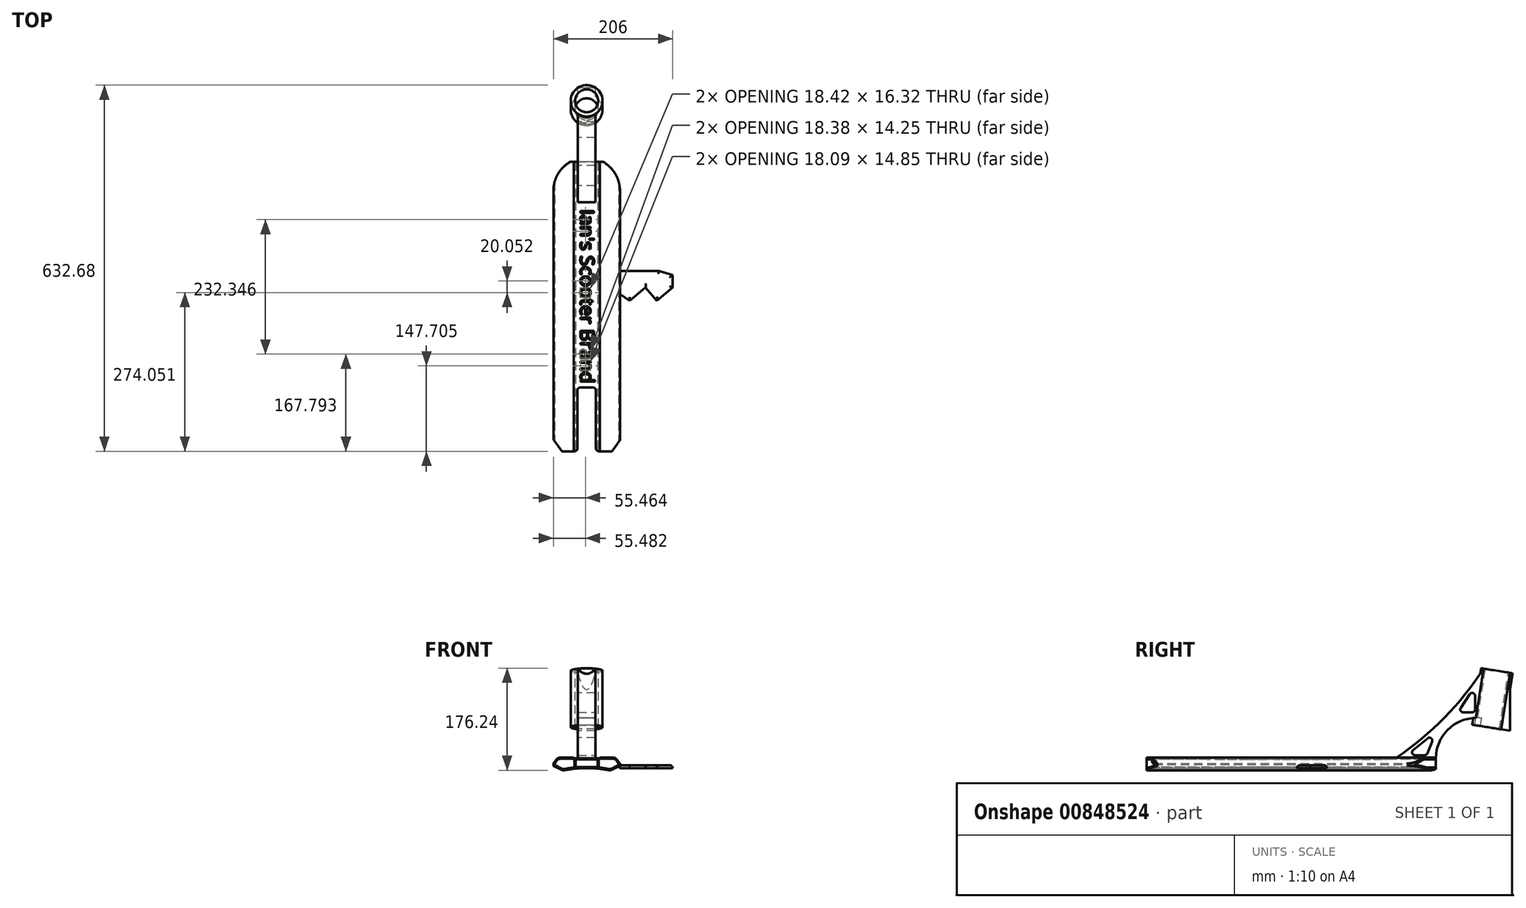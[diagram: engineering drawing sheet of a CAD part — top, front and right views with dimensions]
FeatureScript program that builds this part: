
annotation { "Feature Type Name" : "Feature", "Feature Type Description" : "" }
export const myFeature = defineFeature(function(context is Context, id is Id, definition is map)
    precondition{}
    {
        {
            var Q0;
            Q0=qCreatedBy(makeId("Front.planeOp"),FACE);
            var sketch = newSketch(context, id + "F0", { "sketchPlane" : qUnion([Q0])});
            skLineSegment(sketch, "E0", {"start": v(0, 52.1) * mm, "end": v(0, -52.5) * mm, "construction": true});
            skLineSegment(sketch, "E1", {"start": v(0, 16.68) * mm, "end": v(22.5, 16.68) * mm});
            skLineSegment(sketch, "E2", {"start": v(22.5, 16.68) * mm, "end": v(22.5, 17.98) * mm});
            skLineSegment(sketch, "E3", {"start": v(22.5, 17.98) * mm, "end": v(50.12, 17.98) * mm});
            skLineSegment(sketch, "E4", {"start": v(50.12, 17.98) * mm, "end": v(57.5, 7.98) * mm});
            skLineSegment(sketch, "E5", {"start": v(57.5, 7.98) * mm, "end": v(57.5, 3.98) * mm});
            skLineSegment(sketch, "E6", {"start": v(57.5, 3.98) * mm, "end": v(41.14, -4.28) * mm});
            skLineSegment(sketch, "E7.MirrorCS", {"start": v(0, 16.68) * mm, "end": v(-22.5, 16.68) * mm});
            skLineSegment(sketch, "E8.MirrorCS", {"start": v(-22.5, 17.98) * mm, "end": v(-50.12, 17.98) * mm});
            skLineSegment(sketch, "E9.MirrorCS", {"start": v(-22.5, 16.68) * mm, "end": v(-22.5, 17.98) * mm});
            skLineSegment(sketch, "E10.MirrorCS", {"start": v(-50.12, 17.98) * mm, "end": v(-57.5, 7.98) * mm});
            skLineSegment(sketch, "E11.MirrorCS", {"start": v(-57.5, 7.98) * mm, "end": v(-57.5, 3.98) * mm});
            skLineSegment(sketch, "E12.MirrorCS", {"start": v(-57.5, 3.98) * mm, "end": v(-41.14, -4.28) * mm});
            skArc(sketch, "E13", {"start": v(41.14, -4.28) * mm, "mid": v(0, 0) * mm, "end": v(-41.14, -4.28) * mm});
            skSolve(sketch);
        }
        {
            var Q0;
            Q0 = qSketchRegion(id + "F0", true);
            extrude(context, id + "F1", {"entities" : qUnion([Q0]), "endBound" : BoundingType.SYMMETRIC, "depth" : 500 * mm, "offsetDistance" : 25 * mm});
        }
        {
            var Q0;
            Q0=makeQuery(id+"F1.opExtrude","CAP_FACE",FACE,{"disambiguationData":[OSD([sQuery(id+"F0.wireOp",EDGE,"E1"),sQuery(id+"F0.wireOp",EDGE,"E2"),sQuery(id+"F0.wireOp",EDGE,"E3"),sQuery(id+"F0.wireOp",EDGE,"E4"),sQuery(id+"F0.wireOp",EDGE,"E5"),sQuery(id+"F0.wireOp",EDGE,"E6"),sQuery(id+"F0.wireOp",EDGE,"E7.MirrorCS"),sQuery(id+"F0.wireOp",EDGE,"E8.MirrorCS"),sQuery(id+"F0.wireOp",EDGE,"E9.MirrorCS"),sQuery(id+"F0.wireOp",EDGE,"E10.MirrorCS"),sQuery(id+"F0.wireOp",EDGE,"E11.MirrorCS"),sQuery(id+"F0.wireOp",EDGE,"E12.MirrorCS"),sQuery(id+"F0.wireOp",EDGE,"E13")])],"isStart":false});
            var sketch = newSketch(context, id + "F2", { "sketchPlane" : qUnion([Q0])});
            skLineSegment(sketch, "E14.bottom", {"start": v(19, 14.68) * mm, "end": v(-19, 14.68) * mm});
            skLineSegment(sketch, "E14.top", {"start": v(19, 1.68) * mm, "end": v(-19, 1.68) * mm});
            skLineSegment(sketch, "E14.left", {"start": v(19, 14.68) * mm, "end": v(19, 1.68) * mm});
            skLineSegment(sketch, "E14.right", {"start": v(-19, 14.68) * mm, "end": v(-19, 1.68) * mm});
            skPoint(sketch, "E14.middle", {"position": v(0, 8.18) * mm});
            skSolve(sketch);
        }
        {
            var Q0;
            Q0=makeQuery(id+"F2.imprint","IMPRINT",FACE,{"disambiguationData":[TD([[makeQuery(id+"F2.imprint","IMPRINT",EDGE,{"derivedFrom":sQuery(id+"F2.wireOp",EDGE,"E14.bottom")}),1.0]])]});
            extrude(context, id + "F3", {"entities" : qUnion([Q0]), "operationType" : NewBodyOperationType.REMOVE, "oppositeDirection" : true, "depth" : 1000 * mm, "offsetDistance" : 25 * mm});
        }
        {
            var Q0;
            Q0=makeQuery(id+"F1.opExtrude","SWEPT_EDGE",EDGE,{"disambiguationData":[OSD([sQuery(id+"F0.wireOp",EDGE,"E8.MirrorCS"),sQuery(id+"F0.wireOp",EDGE,"E9.MirrorCS")])]});
            var Q1;
            Q1=makeQuery(id+"F1.opExtrude","SWEPT_EDGE",EDGE,{"disambiguationData":[OSD([sQuery(id+"F0.wireOp",EDGE,"E2"),sQuery(id+"F0.wireOp",EDGE,"E3")])]});
            fillet(context, id + "F4", {"entities" : qUnion([Q0, Q1]), "radius" : 1 * mm, "tangentPropagation" : true, "allowEdgeOverflow" : false});
        }
        {
            var Q0;
            Q0=makeQuery(id+"F1.opExtrude","SWEPT_EDGE",EDGE,{"disambiguationData":[OSD([sQuery(id+"F0.wireOp",EDGE,"E8.MirrorCS"),sQuery(id+"F0.wireOp",EDGE,"E10.MirrorCS")])]});
            var Q1;
            Q1=makeQuery(id+"F1.opExtrude","SWEPT_EDGE",EDGE,{"disambiguationData":[OSD([sQuery(id+"F0.wireOp",EDGE,"E3"),sQuery(id+"F0.wireOp",EDGE,"E4")])]});
            var Q2;
            Q2=makeQuery(id+"F1.opExtrude","SWEPT_EDGE",EDGE,{"disambiguationData":[OSD([sQuery(id+"F0.wireOp",EDGE,"E6"),sQuery(id+"F0.wireOp",EDGE,"E13")])]});
            var Q3;
            Q3=makeQuery(id+"F1.opExtrude","SWEPT_EDGE",EDGE,{"disambiguationData":[OSD([sQuery(id+"F0.wireOp",EDGE,"E12.MirrorCS"),sQuery(id+"F0.wireOp",EDGE,"E13")])]});
            fillet(context, id + "F5", {"entities" : qUnion([Q0, Q1, Q2, Q3]), "radius" : 9 * mm, "tangentPropagation" : true, "allowEdgeOverflow" : false});
        }
        {
            var Q0;
            Q0=makeQuery(id+"F1.opExtrude","SWEPT_EDGE",EDGE,{"disambiguationData":[OSD([sQuery(id+"F0.wireOp",EDGE,"E10.MirrorCS"),sQuery(id+"F0.wireOp",EDGE,"E11.MirrorCS")])]});
            var Q1;
            Q1=makeQuery(id+"F1.opExtrude","SWEPT_EDGE",EDGE,{"disambiguationData":[OSD([sQuery(id+"F0.wireOp",EDGE,"E11.MirrorCS"),sQuery(id+"F0.wireOp",EDGE,"E12.MirrorCS")])]});
            var Q2;
            Q2=makeQuery(id+"F1.opExtrude","SWEPT_EDGE",EDGE,{"disambiguationData":[OSD([sQuery(id+"F0.wireOp",EDGE,"E4"),sQuery(id+"F0.wireOp",EDGE,"E5")])]});
            var Q3;
            Q3=makeQuery(id+"F1.opExtrude","SWEPT_EDGE",EDGE,{"disambiguationData":[OSD([sQuery(id+"F0.wireOp",EDGE,"E5"),sQuery(id+"F0.wireOp",EDGE,"E6")])]});
            fillet(context, id + "F6", {"entities" : qUnion([Q0, Q1, Q2, Q3]), "radius" : 1 * mm, "tangentPropagation" : true, "allowEdgeOverflow" : false});
        }
        {
            var Q0;
            Q0=makeQuery(id+"F1.opExtrude","CAP_FACE",FACE,{"disambiguationData":[OSD([sQuery(id+"F0.wireOp",EDGE,"E1"),sQuery(id+"F0.wireOp",EDGE,"E2"),sQuery(id+"F0.wireOp",EDGE,"E3"),sQuery(id+"F0.wireOp",EDGE,"E4"),sQuery(id+"F0.wireOp",EDGE,"E5"),sQuery(id+"F0.wireOp",EDGE,"E6"),sQuery(id+"F0.wireOp",EDGE,"E7.MirrorCS"),sQuery(id+"F0.wireOp",EDGE,"E8.MirrorCS"),sQuery(id+"F0.wireOp",EDGE,"E9.MirrorCS"),sQuery(id+"F0.wireOp",EDGE,"E10.MirrorCS"),sQuery(id+"F0.wireOp",EDGE,"E11.MirrorCS"),sQuery(id+"F0.wireOp",EDGE,"E12.MirrorCS"),sQuery(id+"F0.wireOp",EDGE,"E13")])],"isStart":false});
            var sketch = newSketch(context, id + "F7", { "sketchPlane" : qUnion([Q0])});
            skArc(sketch, "E15.0", {"start": v(-21, 0.9) * mm, "mid": v(-29.8, -0.2) * mm, "end": v(-38.53, -1.7) * mm});
            skArc(sketch, "E15.1", {"start": v(-43.02, -1.09) * mm, "mid": v(-40.83, -1.77) * mm, "end": v(-38.53, -1.7) * mm});
            skLineSegment(sketch, "E15.2", {"start": v(-55.5, 5.21) * mm, "end": v(-43.02, -1.09) * mm});
            skLineSegment(sketch, "E15.3", {"start": v(-23.5, 15.98) * mm, "end": v(-45.57, 15.98) * mm});
            skArc(sketch, "E15.4", {"start": v(-45.57, 15.98) * mm, "mid": v(-48.73, 15.23) * mm, "end": v(-51.2, 13.14) * mm});
            skLineSegment(sketch, "E15.5", {"start": v(-51.2, 13.14) * mm, "end": v(-55.5, 7.32) * mm});
            skLineSegment(sketch, "E15.6", {"start": v(-55.5, 7.32) * mm, "end": v(-55.5, 5.21) * mm});
            skLineSegment(sketch, "E16.0", {"start": v(-21, 14.68) * mm, "end": v(-21, 0.54) * mm});
            skLineSegment(sketch, "E17.0", {"start": v(-22.5, 14.68) * mm, "end": v(-21, 14.68) * mm});
            skLineSegment(sketch, "E18", {"start": v(-23.5, 15.98) * mm, "end": v(-22.5, 14.68) * mm});
            skLineSegment(sketch, "E19.MirrorCS", {"start": v(21, 14.68) * mm, "end": v(21, 0.54) * mm});
            skLineSegment(sketch, "E20.MirrorCS", {"start": v(22.5, 14.68) * mm, "end": v(21, 14.68) * mm});
            skLineSegment(sketch, "E21.MirrorCS", {"start": v(23.5, 15.98) * mm, "end": v(45.57, 15.98) * mm});
            skArc(sketch, "E22.MirrorCS", {"start": v(45.57, 15.98) * mm, "mid": v(48.73, 15.23) * mm, "end": v(51.2, 13.14) * mm});
            skLineSegment(sketch, "E23.MirrorCS", {"start": v(51.2, 13.14) * mm, "end": v(55.5, 7.32) * mm});
            skLineSegment(sketch, "E24.MirrorCS", {"start": v(23.5, 15.98) * mm, "end": v(22.5, 14.68) * mm});
            skLineSegment(sketch, "E25.MirrorCS", {"start": v(55.5, 5.21) * mm, "end": v(43.02, -1.09) * mm});
            skArc(sketch, "E26.MirrorCS", {"start": v(21, 0.9) * mm, "mid": v(29.8, -0.2) * mm, "end": v(38.53, -1.7) * mm});
            skArc(sketch, "E27.MirrorCS", {"start": v(43.02, -1.09) * mm, "mid": v(40.83, -1.77) * mm, "end": v(38.53, -1.7) * mm});
            skLineSegment(sketch, "E28.MirrorCS", {"start": v(55.5, 7.32) * mm, "end": v(55.5, 5.21) * mm});
            skSolve(sketch);
        }
        {
            var Q0;
            {var subQ0=sQuery(id+"F7.wireOp",EDGE,"E15.0");Q0=makeQuery(id+"F7.imprint","IMPRINT",FACE,{"disambiguationData":[TD([[makeQuery(id+"F7.imprint","IMPRINT",EDGE,{"derivedFrom":subQ0}),-1.0]])]});}
            var Q1;
            {var subQ0=sQuery(id+"F7.wireOp",EDGE,"E20.MirrorCS");Q1=makeQuery(id+"F7.imprint","IMPRINT",FACE,{"disambiguationData":[TD([[makeQuery(id+"F7.imprint","IMPRINT",EDGE,{"derivedFrom":subQ0}),1.0]])]});}
            extrude(context, id + "F8", {"entities" : qUnion([Q0, Q1]), "operationType" : NewBodyOperationType.REMOVE, "oppositeDirection" : true, "depth" : 1000 * mm, "offsetDistance" : 25 * mm});
        }
        {
            var Q0;
            Q0=makeQuery(id+"F1.opExtrude","SWEPT_FACE",FACE,{"disambiguationData":[OSD([sQuery(id+"F0.wireOp",EDGE,"E8.MirrorCS")])]});
            var sketch = newSketch(context, id + "F9", { "sketchPlane" : qUnion([Q0])});
            skCircle(sketch, "E29", {"center": v(0, 200) * mm, "radius": 57.5 * mm});
            skLineSegment(sketch, "E30", {"start": v(-57.5, 200) * mm, "end": v(-57.5, 280) * mm});
            skLineSegment(sketch, "E31", {"start": v(-57.5, 280) * mm, "end": v(57.5, 280) * mm});
            skLineSegment(sketch, "E32", {"start": v(57.5, 280) * mm, "end": v(57.5, 200) * mm});
            skSolve(sketch);
        }
        {
            var Q0;
            {var subQ0=sQuery(id+"F9.wireOp",EDGE,"E30");Q0=makeQuery(id+"F9.imprint","IMPRINT",FACE,{"disambiguationData":[TD([[makeQuery(id+"F9.imprint","IMPRINT",EDGE,{"derivedFrom":subQ0}),-1.0]])]});}
            var Q1;
            {var subQ0=sQuery(id+"F9.wireOp",EDGE,"E29");var subQ1=sQuery(id+"F0.wireOp",EDGE,"E8.MirrorCS");var subQ2=makeQuery(id+"F1.opExtrude","CAP_EDGE",EDGE,{"disambiguationData":[OSD([subQ1])],"isStart":true});var subQ3=makeQuery(id+"F9.imprint","INTERSECT",VERTEX,{"derivedFrom":[subQ2,subQ0]});Q1=makeQuery(id+"F9.imprint","IMPRINT",FACE,{"disambiguationData":[TD([[makeQuery(id+"F9.imprint","IMPRINT",EDGE,{"disambiguationData":[TD([[subQ3,-1.0]])],"derivedFrom":subQ0}),-1.0]])]});}
            extrude(context, id + "F10", {"entities" : qUnion([Q0, Q1]), "operationType" : NewBodyOperationType.REMOVE, "endBound" : BoundingType.THROUGH_ALL, "depth" : 25 * mm, "offsetDistance" : 25 * mm, "hasSecondDirection" : true, "secondDirectionBound" : SecondDirectionBoundingType.THROUGH_ALL, "secondDirectionOppositeDirection" : true, "secondDirectionDepth" : 25 * mm});
        }
        {
            var Q0;
            Q0=makeQuery(id+"F1.opExtrude","SWEPT_FACE",FACE,{"disambiguationData":[OSD([sQuery(id+"F0.wireOp",EDGE,"E8.MirrorCS")])]});
            var sketch = newSketch(context, id + "F11", { "sketchPlane" : qUnion([Q0])});
            skLineSegment(sketch, "E33", {"start": v(-16, -250.16) * mm, "end": v(-16, -140) * mm});
            skLineSegment(sketch, "E34", {"start": v(-16, -140) * mm, "end": v(16, -140) * mm});
            skLineSegment(sketch, "E35", {"start": v(16, -140) * mm, "end": v(16, -250) * mm});
            skLineSegment(sketch, "E36", {"start": v(16, -250) * mm, "end": v(43.9, -250) * mm});
            skLineSegment(sketch, "E37", {"start": v(43.9, -250) * mm, "end": v(68.6, -216) * mm});
            skLineSegment(sketch, "E38", {"start": v(68.6, -216) * mm, "end": v(68.6, -346) * mm});
            skLineSegment(sketch, "E39", {"start": v(68.6, -346) * mm, "end": v(-67.4, -346) * mm});
            skLineSegment(sketch, "E40", {"start": v(-67.4, -346) * mm, "end": v(-67.4, -216) * mm});
            skLineSegment(sketch, "E41", {"start": v(-67.4, -216) * mm, "end": v(-42.7, -250) * mm});
            skLineSegment(sketch, "E42", {"start": v(-42.7, -250) * mm, "end": v(-16, -250.16) * mm});
            skSolve(sketch);
        }
        {
            var Q0;
            Q0=makeQuery(id+"F11.imprint","IMPRINT",FACE,{"disambiguationData":[TD([[makeQuery(id+"F11.imprint","IMPRINT",EDGE,{"derivedFrom":sQuery(id+"F11.wireOp",EDGE,"E33")}),-1.0]])]});
            var Q1;
            {var subQ0=sQuery(id+"F11.wireOp",EDGE,"E41");var subQ1=sQuery(id+"F0.wireOp",EDGE,"E8.MirrorCS");var subQ2=makeQuery(id+"F1.opExtrude","CAP_EDGE",EDGE,{"disambiguationData":[OSD([subQ1])],"isStart":false});var subQ3=makeQuery(id+"F11.imprint","INTERSECT",VERTEX,{"derivedFrom":[subQ2,subQ0,sQuery(id+"F11.wireOp",EDGE,"E42")]});Q1=makeQuery(id+"F11.imprint","IMPRINT",FACE,{"disambiguationData":[TD([[makeQuery(id+"F11.imprint","IMPRINT",EDGE,{"disambiguationData":[TD([[subQ3,1.0]])],"derivedFrom":subQ0}),-1.0]])]});}
            extrude(context, id + "F12", {"entities" : qUnion([Q0, Q1]), "operationType" : NewBodyOperationType.REMOVE, "endBound" : BoundingType.THROUGH_ALL, "oppositeDirection" : true, "depth" : 25 * mm, "offsetDistance" : 25 * mm, "hasSecondDirection" : true, "secondDirectionBound" : SecondDirectionBoundingType.THROUGH_ALL, "secondDirectionOppositeDirection" : false, "secondDirectionDepth" : 25 * mm});
        }
        {
            var Q0;
            {var subQ0=sQuery(id+"F11.wireOp",EDGE,"E34");var subQ1=sQuery(id+"F11.wireOp",EDGE,"E33");Q0=makeQuery(id+"F12.boolean.opBoolean","COPY",EDGE,{"disambiguationData":[TD([makeQuery(id+"F3.boolean.opBoolean","COPY",FACE,{"derivedFrom":makeQuery(id+"F3.opExtrude","SWEPT_FACE",FACE,{"disambiguationData":[OSD([sQuery(id+"F2.wireOp",EDGE,"E14.bottom")])]})})])],"derivedFrom":makeQuery(id+"F12.opExtrude","SWEPT_EDGE",EDGE,{"disambiguationData":[OSD([subQ1,subQ0])]})});}
            var Q1;
            {var subQ0=sQuery(id+"F11.wireOp",EDGE,"E33");var subQ1=sQuery(id+"F11.wireOp",EDGE,"E34");Q1=makeQuery(id+"F12.boolean.opBoolean","COPY",EDGE,{"disambiguationData":[TD([makeQuery(id+"F1.opExtrude","SWEPT_FACE",FACE,{"disambiguationData":[OSD([sQuery(id+"F0.wireOp",EDGE,"E13")])]})])],"derivedFrom":makeQuery(id+"F12.opExtrude","SWEPT_EDGE",EDGE,{"disambiguationData":[OSD([subQ0,subQ1])]})});}
            var Q2;
            {var subQ0=sQuery(id+"F11.wireOp",EDGE,"E34");var subQ1=sQuery(id+"F11.wireOp",EDGE,"E35");Q2=makeQuery(id+"F12.boolean.opBoolean","COPY",EDGE,{"disambiguationData":[TD([makeQuery(id+"F3.boolean.opBoolean","COPY",FACE,{"derivedFrom":makeQuery(id+"F3.opExtrude","SWEPT_FACE",FACE,{"disambiguationData":[OSD([sQuery(id+"F2.wireOp",EDGE,"E14.bottom")])]})})])],"derivedFrom":makeQuery(id+"F12.opExtrude","SWEPT_EDGE",EDGE,{"disambiguationData":[OSD([subQ0,subQ1])]})});}
            var Q3;
            {var subQ0=sQuery(id+"F11.wireOp",EDGE,"E35");var subQ1=sQuery(id+"F11.wireOp",EDGE,"E34");Q3=makeQuery(id+"F12.boolean.opBoolean","COPY",EDGE,{"disambiguationData":[TD([makeQuery(id+"F1.opExtrude","SWEPT_FACE",FACE,{"disambiguationData":[OSD([sQuery(id+"F0.wireOp",EDGE,"E13")])]})])],"derivedFrom":makeQuery(id+"F12.opExtrude","SWEPT_EDGE",EDGE,{"disambiguationData":[OSD([subQ1,subQ0])]})});}
            var Q4;
            {var subQ2=sQuery(id+"F11.wireOp",EDGE,"E35");Q4=makeQuery(id+"F12.boolean.opBoolean","COPY",EDGE,{"disambiguationData":[TD([makeQuery(id+"F3.boolean.opBoolean","COPY",FACE,{"derivedFrom":makeQuery(id+"F3.opExtrude","SWEPT_FACE",FACE,{"disambiguationData":[OSD([sQuery(id+"F2.wireOp",EDGE,"E14.bottom")])]})})])],"derivedFrom":makeQuery(id+"F12.opExtrude","SWEPT_EDGE",EDGE,{"disambiguationData":[OSD([subQ2,sQuery(id+"F11.wireOp",EDGE,"E36")])]})});}
            var Q5;
            Q5=makeQuery(id+"F12.boolean.opBoolean","INTERSECT",EDGE,{"disambiguationData":[OD(0.0)],"derivedFrom":[makeQuery(id+"F1.opExtrude","CAP_FACE",FACE,{"disambiguationData":[OSD([sQuery(id+"F0.wireOp",EDGE,"E1"),sQuery(id+"F0.wireOp",EDGE,"E2"),sQuery(id+"F0.wireOp",EDGE,"E3"),sQuery(id+"F0.wireOp",EDGE,"E4"),sQuery(id+"F0.wireOp",EDGE,"E5"),sQuery(id+"F0.wireOp",EDGE,"E6"),sQuery(id+"F0.wireOp",EDGE,"E7.MirrorCS"),sQuery(id+"F0.wireOp",EDGE,"E8.MirrorCS"),sQuery(id+"F0.wireOp",EDGE,"E9.MirrorCS"),sQuery(id+"F0.wireOp",EDGE,"E10.MirrorCS"),sQuery(id+"F0.wireOp",EDGE,"E11.MirrorCS"),sQuery(id+"F0.wireOp",EDGE,"E12.MirrorCS"),sQuery(id+"F0.wireOp",EDGE,"E13")])],"isStart":false}),makeQuery(id+"F12.opExtrude","SWEPT_FACE",FACE,{"disambiguationData":[OSD([sQuery(id+"F11.wireOp",EDGE,"E33")])]})]});
            fillet(context, id + "F13", {"entities" : qUnion([Q0, Q1, Q2, Q3, Q4, Q5]), "radius" : 5 * mm, "tangentPropagation" : true, "allowEdgeOverflow" : false});
        }
        {
            var Q0;
            Q0=qCreatedBy(makeId("Right.planeOp"),FACE);
            var sketch = newSketch(context, id + "F14", { "sketchPlane" : qUnion([Q0])});
            skLineSegment(sketch, "E43", {"start": v(250.22, 16.68) * mm, "end": v(180.22, 16.68) * mm});
            skLineSegment(sketch, "E44", {"start": v(332.8, 85.54) * mm, "end": v(332.8, 71.7) * mm});
            skLineSegment(sketch, "E45", {"start": v(332.8, 71.7) * mm, "end": v(378.23, 64.5) * mm});
            skLineSegment(sketch, "E46", {"start": v(378.23, 64.5) * mm, "end": v(378.23, 164.5) * mm});
            skLineSegment(sketch, "E47", {"start": v(378.23, 164.5) * mm, "end": v(332.8, 171.7) * mm});
            skArc(sketch, "E48", {"start": v(180.22, 16.68) * mm, "mid": v(264.25, 86.57) * mm, "end": v(332.8, 171.7) * mm});
            skArc(sketch, "E49", {"start": v(332.8, 85.54) * mm, "mid": v(275.4, 70.44) * mm, "end": v(250.22, 16.68) * mm});
            skSolve(sketch);
        }
        {
            var Q0;
            Q0=makeQuery(id+"F14.imprint","IMPRINT",FACE,{"disambiguationData":[TD([[makeQuery(id+"F14.imprint","IMPRINT",EDGE,{"derivedFrom":sQuery(id+"F14.wireOp",EDGE,"E43")}),-1.0]])]});
            extrude(context, id + "F15", {"entities" : qUnion([Q0]), "operationType" : NewBodyOperationType.ADD, "endBound" : BoundingType.SYMMETRIC, "depth" : 30 * mm, "offsetDistance" : 25 * mm});
        }
        {
            var Q0;
            Q0=makeQuery(id+"F15.opExtrude","SWEPT_FACE",FACE,{"disambiguationData":[OSD([sQuery(id+"F14.wireOp",EDGE,"E47")])]});
            var sketch = newSketch(context, id + "F16", { "sketchPlane" : qUnion([Q0])});
            skCircle(sketch, "E50", {"center": v(0, 324.85) * mm, "radius": 27.5 * mm});
            skPoint(sketch, "E50.centerSnap0", {"position": v(15, 324.85) * mm});
            skSolve(sketch);
        }
        {
            var Q0;
            Q0=makeQuery(id+"F16.imprint","IMPRINT",FACE,{"disambiguationData":[TD([[makeQuery(id+"F16.imprint","IMPRINT",EDGE,{"derivedFrom":sQuery(id+"F16.wireOp",EDGE,"E50")}),1.0]])]});
            var Q1;
            Q1=makeQuery(id+"F15.opExtrude","SWEPT_FACE",FACE,{"disambiguationData":[OSD([sQuery(id+"F14.wireOp",EDGE,"E45")])]});
            extrude(context, id + "F17", {"entities" : qUnion([Q0]), "operationType" : NewBodyOperationType.ADD, "endBound" : BoundingType.UP_TO_SURFACE, "oppositeDirection" : true, "depth" : 25 * mm, "endBoundEntityFace" : qUnion([Q1]), "offsetDistance" : 25 * mm});
        }
        {
            var Q0;
            {var subQ0=sQuery(id+"F14.wireOp",EDGE,"E47");Q0=makeQuery(id+"F17.boolean.opBoolean","MERGE",FACE,{"derivedFrom":[makeQuery(id+"F15.opExtrude","SWEPT_FACE",FACE,{"disambiguationData":[OSD([subQ0])]}),makeQuery(id+"F17.opExtrude","CAP_FACE",FACE,{"disambiguationData":[OSD([sQuery(id+"F14.wireOp",EDGE,"E46"),subQ0,sQuery(id+"F14.wireOp",EDGE,"E48"),sQuery(id+"F16.wireOp",EDGE,"E50")])],"isStart":true})]});}
            var sketch = newSketch(context, id + "F18", { "sketchPlane" : qUnion([Q0])});
            skPoint(sketch, "E51", {"position": v(0, 324.85) * mm});
            skSolve(sketch);
        }
        {
            var Q0;
            Q0=sQuery(id+"F18.wireOp",VERTEX,"E51");
            var Q1;
            Q1=makeQuery(id+"F1.opExtrude","SWEPT_BODY",BODY,{"disambiguationData":[OSD([sQuery(id+"F0.wireOp",EDGE,"E1"),sQuery(id+"F0.wireOp",EDGE,"E2"),sQuery(id+"F0.wireOp",EDGE,"E3"),sQuery(id+"F0.wireOp",EDGE,"E4"),sQuery(id+"F0.wireOp",EDGE,"E5"),sQuery(id+"F0.wireOp",EDGE,"E6"),sQuery(id+"F0.wireOp",EDGE,"E7.MirrorCS"),sQuery(id+"F0.wireOp",EDGE,"E8.MirrorCS"),sQuery(id+"F0.wireOp",EDGE,"E9.MirrorCS"),sQuery(id+"F0.wireOp",EDGE,"E10.MirrorCS"),sQuery(id+"F0.wireOp",EDGE,"E11.MirrorCS"),sQuery(id+"F0.wireOp",EDGE,"E12.MirrorCS"),sQuery(id+"F0.wireOp",EDGE,"E13")])]});
            hole(context, id + "F19", {"style" : HoleStyle.SIMPLE, "endStyle" : HoleEndStyle.THROUGH, "holeDiameter" : 40 * mm, "majorDiameter" : 5 * mm, "isTappedThrough" : true, "tappedDepth" : 12 * mm, "tapClearance" : 3, "locations" : qUnion([Q0]), "scope" : qUnion([Q1])});
        }
        {
            var Q0;
            Q0=makeQuery(id+"F8.boolean.opBoolean","COPY",FACE,{"derivedFrom":makeQuery(id+"F8.opExtrude","SWEPT_FACE",FACE,{"disambiguationData":[OSD([sQuery(id+"F7.wireOp",EDGE,"E19.MirrorCS")])]})});
            var sketch = newSketch(context, id + "F20", { "sketchPlane" : qUnion([Q0])});
            skPoint(sketch, "E52", {"position": v(-236, 10.9) * mm});
            skSolve(sketch);
        }
        {
            var Q0;
            Q0=sQuery(id+"F20.wireOp",VERTEX,"E52");
            var Q1;
            Q1=makeQuery(id+"F1.opExtrude","SWEPT_BODY",BODY,{"disambiguationData":[OSD([sQuery(id+"F0.wireOp",EDGE,"E1"),sQuery(id+"F0.wireOp",EDGE,"E2"),sQuery(id+"F0.wireOp",EDGE,"E3"),sQuery(id+"F0.wireOp",EDGE,"E4"),sQuery(id+"F0.wireOp",EDGE,"E5"),sQuery(id+"F0.wireOp",EDGE,"E6"),sQuery(id+"F0.wireOp",EDGE,"E7.MirrorCS"),sQuery(id+"F0.wireOp",EDGE,"E8.MirrorCS"),sQuery(id+"F0.wireOp",EDGE,"E9.MirrorCS"),sQuery(id+"F0.wireOp",EDGE,"E10.MirrorCS"),sQuery(id+"F0.wireOp",EDGE,"E11.MirrorCS"),sQuery(id+"F0.wireOp",EDGE,"E12.MirrorCS"),sQuery(id+"F0.wireOp",EDGE,"E13")])]});
            hole(context, id + "F21", {"style" : HoleStyle.SIMPLE, "endStyle" : HoleEndStyle.BLIND, "holeDiameter" : 8 * mm, "majorDiameter" : 5 * mm, "holeDepth" : 50 * mm, "isTappedThrough" : true, "tappedDepth" : 12 * mm, "tapClearance" : 3, "locations" : qUnion([Q0]), "scope" : qUnion([Q1])});
        }
        {
            var Q0;
            {var subQ0=sQuery(id+"F14.wireOp",EDGE,"E48");var subQ1=sQuery(id+"F14.wireOp",EDGE,"E43");var subQ4=sQuery(id+"F14.wireOp",EDGE,"E49");Q0=makeQuery(id+"F17.boolean.opBoolean","SPLIT",FACE,{"disambiguationData":[TD([makeQuery(id+"F15.opExtrude","SWEPT_FACE",FACE,{"disambiguationData":[OSD([subQ1])]})])],"derivedFrom":makeQuery(id+"F15.opExtrude","CAP_FACE",FACE,{"disambiguationData":[OSD([subQ1,sQuery(id+"F14.wireOp",EDGE,"E44"),sQuery(id+"F14.wireOp",EDGE,"E45"),sQuery(id+"F14.wireOp",EDGE,"E46"),sQuery(id+"F14.wireOp",EDGE,"E47"),subQ0,subQ4])],"isStart":false})});}
            var sketch = newSketch(context, id + "F22", { "sketchPlane" : qUnion([Q0])});
            skLineSegment(sketch, "E53", {"start": v(200, 22.2) * mm, "end": v(234, 22.2) * mm});
            skPoint(sketch, "E53.startSnap0", {"position": v(215.11, 16.68) * mm});
            skLineSegment(sketch, "E54", {"start": v(234, 22.2) * mm, "end": v(251, 63.88) * mm});
            skLineSegment(sketch, "E55", {"start": v(251, 63.88) * mm, "end": v(200, 22.2) * mm});
            skLineSegment(sketch, "E56", {"start": v(287.87, 96.3) * mm, "end": v(317.87, 96.3) * mm});
            skLineSegment(sketch, "E57", {"start": v(317.87, 96.3) * mm, "end": v(317.87, 141.3) * mm});
            skLineSegment(sketch, "E58", {"start": v(317.87, 141.3) * mm, "end": v(287.87, 96.3) * mm});
            skSolve(sketch);
        }
        {
            var Q0;
            Q0=makeQuery(id+"F22.imprint","IMPRINT",FACE,{"disambiguationData":[TD([[makeQuery(id+"F22.imprint","IMPRINT",EDGE,{"derivedFrom":sQuery(id+"F22.wireOp",EDGE,"E56")}),1.0]])]});
            var Q1;
            Q1=makeQuery(id+"F22.imprint","IMPRINT",FACE,{"disambiguationData":[TD([[makeQuery(id+"F22.imprint","IMPRINT",EDGE,{"derivedFrom":sQuery(id+"F22.wireOp",EDGE,"E53")}),1.0]])]});
            extrude(context, id + "F23", {"entities" : qUnion([Q0, Q1]), "operationType" : NewBodyOperationType.REMOVE, "endBound" : BoundingType.THROUGH_ALL, "oppositeDirection" : true, "depth" : 25 * mm, "offsetDistance" : 25 * mm});
        }
        {
            var Q0;
            Q0=makeQuery(id+"F23.boolean.opBoolean","COPY",EDGE,{"derivedFrom":makeQuery(id+"F23.opExtrude","SWEPT_EDGE",EDGE,{"disambiguationData":[OSD([sQuery(id+"F22.wireOp",EDGE,"E57"),sQuery(id+"F22.wireOp",EDGE,"E58")])]})});
            var Q1;
            Q1=makeQuery(id+"F23.boolean.opBoolean","COPY",EDGE,{"derivedFrom":makeQuery(id+"F23.opExtrude","SWEPT_EDGE",EDGE,{"disambiguationData":[OSD([sQuery(id+"F22.wireOp",EDGE,"E56"),sQuery(id+"F22.wireOp",EDGE,"E58")])]})});
            var Q2;
            Q2=makeQuery(id+"F23.boolean.opBoolean","COPY",EDGE,{"derivedFrom":makeQuery(id+"F23.opExtrude","SWEPT_EDGE",EDGE,{"disambiguationData":[OSD([sQuery(id+"F22.wireOp",EDGE,"E56"),sQuery(id+"F22.wireOp",EDGE,"E57")])]})});
            var Q3;
            Q3=makeQuery(id+"F23.boolean.opBoolean","COPY",EDGE,{"derivedFrom":makeQuery(id+"F23.opExtrude","SWEPT_EDGE",EDGE,{"disambiguationData":[OSD([sQuery(id+"F22.wireOp",EDGE,"E53"),sQuery(id+"F22.wireOp",EDGE,"E54")])]})});
            var Q4;
            Q4=makeQuery(id+"F23.boolean.opBoolean","COPY",EDGE,{"derivedFrom":makeQuery(id+"F23.opExtrude","SWEPT_EDGE",EDGE,{"disambiguationData":[OSD([sQuery(id+"F22.wireOp",EDGE,"E53"),sQuery(id+"F22.wireOp",EDGE,"E55")])]})});
            var Q5;
            Q5=makeQuery(id+"F23.boolean.opBoolean","COPY",EDGE,{"derivedFrom":makeQuery(id+"F23.opExtrude","SWEPT_EDGE",EDGE,{"disambiguationData":[OSD([sQuery(id+"F22.wireOp",EDGE,"E54"),sQuery(id+"F22.wireOp",EDGE,"E55")])]})});
            fillet(context, id + "F24", {"entities" : qUnion([Q0, Q1, Q2, Q3, Q4, Q5]), "radius" : 5 * mm, "tangentPropagation" : true, "allowEdgeOverflow" : false});
        }
        {
            var Q0;
            Q0=qCreatedBy(makeId("Top.planeOp"),FACE);
            var sketch = newSketch(context, id + "F25", { "sketchPlane" : qUnion([Q0])});
            skText(sketch, "E59", { "text": "Ian\'s Scooter Brand", "fontName": "OpenSans-Regular.ttf"});
            const initialGuessF25  = {"E59": [-0.0109, 0.16804, 0, -1, 0.0239]};
            skSetInitialGuess(sketch, initialGuessF25);
            skSolve(sketch);
        }
        {
            var Q0;
            Q0 = qSketchRegion(id + "F25", true);
            extrude(context, id + "F26", {"entities" : qUnion([Q0]), "operationType" : NewBodyOperationType.REMOVE, "endBound" : BoundingType.SYMMETRIC, "oppositeDirection" : true, "depth" : 100 * mm, "offsetDistance" : 25 * mm});
        }
        {
            var Q0;
            Q0=qCreatedBy(makeId("Top.planeOp"),FACE);
            var sketch = newSketch(context, id + "F27", { "sketchPlane" : qUnion([Q0])});
            skLineSegment(sketch, "E60", {"start": v(58.02, 61.74) * mm, "end": v(124.71, 61.74) * mm});
            skLineSegment(sketch, "E61", {"start": v(124.71, 61.74) * mm, "end": v(148.5, 54.33) * mm});
            skLineSegment(sketch, "E62", {"start": v(148.5, 54.33) * mm, "end": v(148.5, 32.88) * mm});
            skLineSegment(sketch, "E63", {"start": v(148.5, 32.88) * mm, "end": v(121.2, 9.87) * mm});
            skLineSegment(sketch, "E64", {"start": v(121.2, 9.87) * mm, "end": v(101.8, 32.88) * mm});
            skLineSegment(sketch, "E65", {"start": v(101.8, 32.88) * mm, "end": v(74.5, 9.87) * mm});
            skLineSegment(sketch, "E66", {"start": v(74.5, 9.87) * mm, "end": v(57.24, 21.94) * mm});
            skLineSegment(sketch, "E67", {"start": v(57.24, 21.94) * mm, "end": v(57.24, 61.74) * mm});
            skLineSegment(sketch, "E68", {"start": v(57.24, 61.74) * mm, "end": v(58.02, 61.74) * mm});
            skSolve(sketch);
        }
        {
            var Q0;
            Q0 = qSketchRegion(id + "F27", true);
            extrude(context, id + "F28", {"entities" : qUnion([Q0]), "operationType" : NewBodyOperationType.ADD, "depth" : 5 * mm, "offsetDistance" : 25 * mm});
        }
        {
            var Q0;
            Q0=makeQuery(id+"F28.opExtrude","CAP_EDGE",EDGE,{"disambiguationData":[OSD([sQuery(id+"F27.wireOp",EDGE,"E61")])],"isStart":false});
            var Q1;
            Q1=makeQuery(id+"F28.opExtrude","CAP_EDGE",EDGE,{"disambiguationData":[OSD([sQuery(id+"F27.wireOp",EDGE,"E60"),sQuery(id+"F27.wireOp",EDGE,"E68")])],"isStart":false});
            var Q2;
            Q2=makeQuery(id+"F28.opExtrude","CAP_EDGE",EDGE,{"disambiguationData":[OSD([sQuery(id+"F27.wireOp",EDGE,"E62")])],"isStart":false});
            var Q3;
            Q3=makeQuery(id+"F28.opExtrude","CAP_EDGE",EDGE,{"disambiguationData":[OSD([sQuery(id+"F27.wireOp",EDGE,"E65")])],"isStart":false});
            var Q4;
            Q4=makeQuery(id+"F28.opExtrude","CAP_EDGE",EDGE,{"disambiguationData":[OSD([sQuery(id+"F27.wireOp",EDGE,"E66")])],"isStart":false});
            var Q5;
            Q5=makeQuery(id+"F28.opExtrude","CAP_EDGE",EDGE,{"disambiguationData":[OSD([sQuery(id+"F27.wireOp",EDGE,"E63")])],"isStart":false});
            var Q6;
            Q6=makeQuery(id+"F28.opExtrude","CAP_EDGE",EDGE,{"disambiguationData":[OSD([sQuery(id+"F27.wireOp",EDGE,"E64")])],"isStart":false});
            var Q7;
            Q7=makeQuery(id+"FouIxVYY4MaG2HT_1.1.F28.opExtrude","CAP_EDGE",EDGE,{"disambiguationData":[OSD([sQuery(id+"F27.wireOp",EDGE,"E61")])],"isStart":false});
            var Q8;
            Q8=makeQuery(id+"FouIxVYY4MaG2HT_1.1.F28.opExtrude","CAP_EDGE",EDGE,{"disambiguationData":[OSD([sQuery(id+"F27.wireOp",EDGE,"E62")])],"isStart":false});
            var Q9;
            Q9=makeQuery(id+"FouIxVYY4MaG2HT_1.1.F28.opExtrude","CAP_EDGE",EDGE,{"disambiguationData":[OSD([sQuery(id+"F27.wireOp",EDGE,"E63")])],"isStart":false});
            var Q10;
            Q10=makeQuery(id+"FouIxVYY4MaG2HT_1.1.F28.opExtrude","CAP_EDGE",EDGE,{"disambiguationData":[OSD([sQuery(id+"F27.wireOp",EDGE,"E64")])],"isStart":false});
            var Q11;
            Q11=makeQuery(id+"FouIxVYY4MaG2HT_1.1.F28.opExtrude","CAP_EDGE",EDGE,{"disambiguationData":[OSD([sQuery(id+"F27.wireOp",EDGE,"E65")])],"isStart":false});
            var Q12;
            Q12=makeQuery(id+"FouIxVYY4MaG2HT_1.1.F28.opExtrude","CAP_EDGE",EDGE,{"disambiguationData":[OSD([sQuery(id+"F27.wireOp",EDGE,"E66")])],"isStart":false});
            var Q13;
            Q13=makeQuery(id+"FouIxVYY4MaG2HT_1.1.F28.opExtrude","CAP_EDGE",EDGE,{"disambiguationData":[OSD([sQuery(id+"F27.wireOp",EDGE,"E60"),sQuery(id+"F27.wireOp",EDGE,"E68")])],"isStart":false});
            fillet(context, id + "F29", {"entities" : qUnion([Q0, Q1, Q2, Q3, Q4, Q5, Q6, Q7, Q8, Q9, Q10, Q11, Q12, Q13]), "radius" : 5 * mm, "tangentPropagation" : true, "allowEdgeOverflow" : false});
        }
    });
